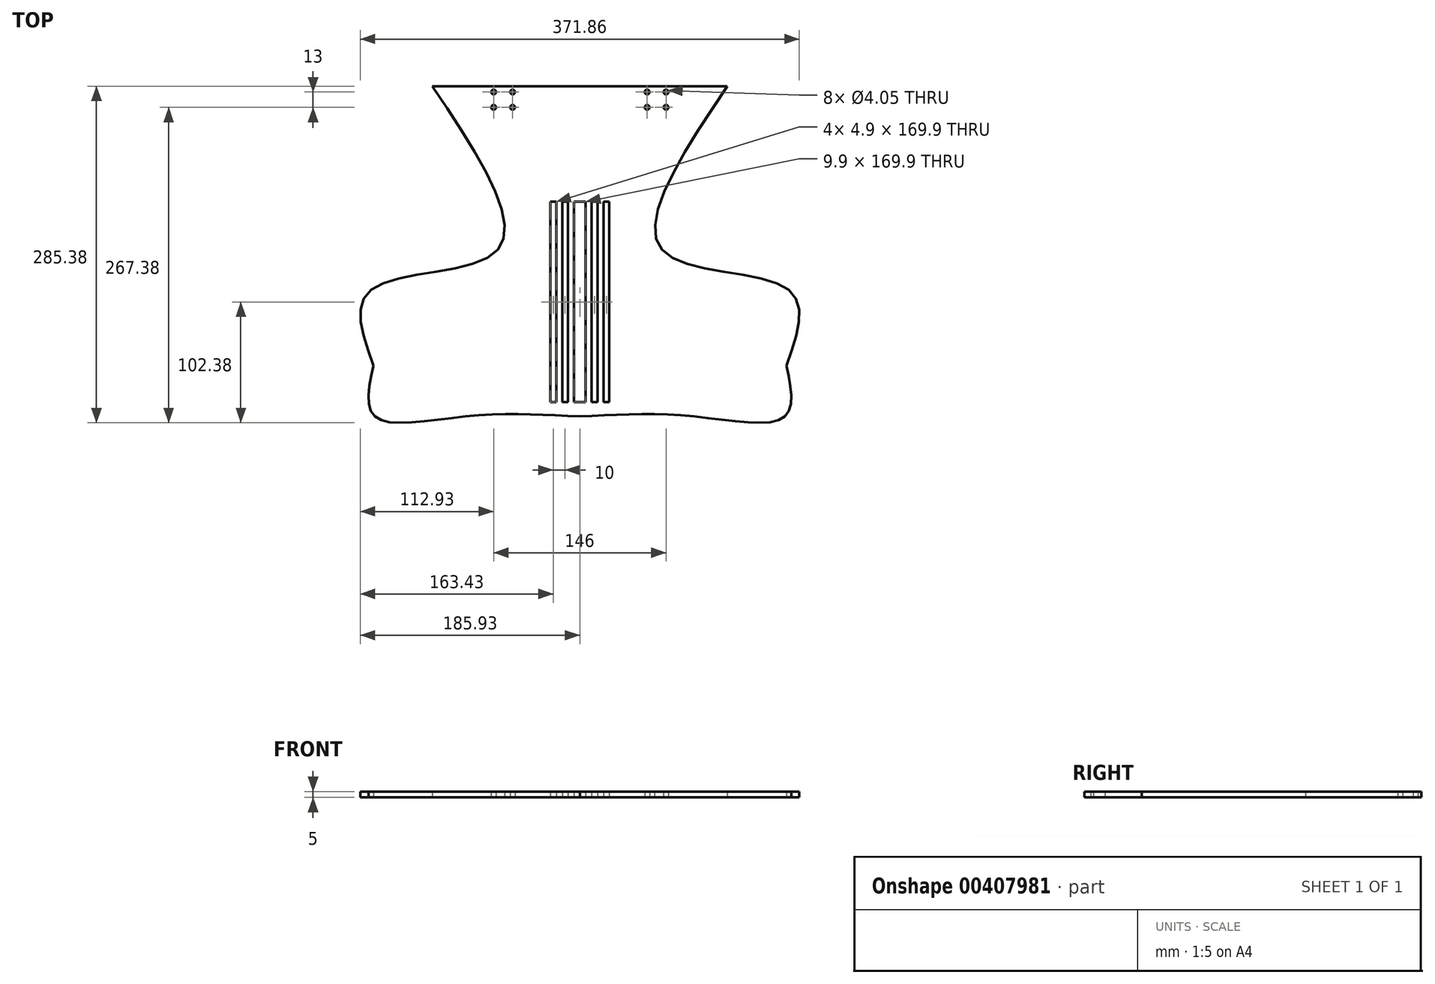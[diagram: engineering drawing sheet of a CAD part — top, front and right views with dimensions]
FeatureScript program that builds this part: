
annotation { "Feature Type Name" : "Feature", "Feature Type Description" : "" }
export const myFeature = defineFeature(function(context is Context, id is Id, definition is map)
    precondition{}
    {
        {
            var Q0;
            Q0=qCreatedBy(makeId("Top.planeOp"),FACE);
            var sketch = newSketch(context, id + "F0", { "sketchPlane" : qUnion([Q0])});
            skLineSegment(sketch, "E0.bottom", {"start": v(-125, 0) * mm, "end": v(125, 0) * mm, "construction": true});
            skLineSegment(sketch, "E0.top", {"start": v(-125, -280) * mm, "end": v(125, -280) * mm, "construction": true});
            skLineSegment(sketch, "E0.left", {"start": v(-125, 0) * mm, "end": v(-125, -280) * mm, "construction": true});
            skLineSegment(sketch, "E0.right", {"start": v(125, 0) * mm, "end": v(125, -280) * mm, "construction": true});
            skFitSpline(sketch, "E1", {"points": [v(-125, 0) * mm, v(-175, -236.88) * mm], "startDerivative": vector(163.58, -419.06) * mm, "endDerivative": vector(5.98, -192.46) * mm});
            skPoint(sketch, "E2", {"position": v(0, -280) * mm});
            skFitSpline(sketch, "E3", {"points": [v(-175, -236.88) * mm, v(0, -280) * mm], "startDerivative": vector(4.02, -129.37) * mm, "endDerivative": vector(290.73, 0) * mm});
            skFitSpline(sketch, "E4.MirrorCS", {"points": [v(125, 0) * mm, v(175, -236.88) * mm], "startDerivative": vector(-163.58, -419.06) * mm, "endDerivative": vector(-5.98, -192.46) * mm});
            skFitSpline(sketch, "E5.MirrorCS", {"points": [v(175, -236.88) * mm, v(0, -280) * mm], "startDerivative": vector(-4.02, -129.37) * mm, "endDerivative": vector(-290.73, 0) * mm});
            skFitSpline(sketch, "E6", {"points": [v(-125, 0) * mm, v(0, 25) * mm], "startDerivative": vector(-31, 79.42) * mm, "endDerivative": vector(148.36, 0.98) * mm});
            skFitSpline(sketch, "E7.MirrorCS", {"points": [v(125, 0) * mm, v(0, 25) * mm], "startDerivative": vector(31, 79.42) * mm, "endDerivative": vector(-148.36, 0.98) * mm});
            skLineSegment(sketch, "E8.bottom", {"start": v(-10, -88) * mm, "end": v(-5, -88) * mm, "construction": true});
            skLineSegment(sketch, "E8.top", {"start": v(-10, -278) * mm, "end": v(-5, -278) * mm, "construction": true});
            skLineSegment(sketch, "E8.left", {"start": v(-10, -88) * mm, "end": v(-10, -278) * mm, "construction": true});
            skLineSegment(sketch, "E8.right", {"start": v(-5, -88) * mm, "end": v(-5, -278) * mm, "construction": true});
            skLineSegment(sketch, "E9.1.0.0", {"start": v(-20, -88) * mm, "end": v(-20, -278) * mm, "construction": true});
            skLineSegment(sketch, "E9.1.0.1", {"start": v(-15, -88) * mm, "end": v(-15, -278) * mm, "construction": true});
            skLineSegment(sketch, "E9.1.0.2", {"start": v(-20, -88) * mm, "end": v(-15, -88) * mm, "construction": true});
            skLineSegment(sketch, "E9.1.0.3", {"start": v(-20, -278) * mm, "end": v(-15, -278) * mm, "construction": true});
            skLineSegment(sketch, "E9.2.0.0", {"start": v(-30, -88) * mm, "end": v(-30, -278) * mm, "construction": true});
            skLineSegment(sketch, "E9.2.0.1", {"start": v(-25, -88) * mm, "end": v(-25, -278) * mm, "construction": true});
            skLineSegment(sketch, "E9.2.0.2", {"start": v(-30, -88) * mm, "end": v(-25, -88) * mm, "construction": true});
            skLineSegment(sketch, "E9.2.0.3", {"start": v(-30, -278) * mm, "end": v(-25, -278) * mm, "construction": true});
            skLineSegment(sketch, "E9.direction1", {"start": v(-10, -278) * mm, "end": v(-20, -278) * mm, "construction": true});
            skLineSegment(sketch, "E10.MirrorCS", {"start": v(10, -278) * mm, "end": v(20, -278) * mm, "construction": true});
            skLineSegment(sketch, "E11.MirrorCS", {"start": v(20, -278) * mm, "end": v(15, -278) * mm, "construction": true});
            skLineSegment(sketch, "E12.MirrorCS", {"start": v(10, -278) * mm, "end": v(5, -278) * mm, "construction": true});
            skLineSegment(sketch, "E13.MirrorCS", {"start": v(20, -88) * mm, "end": v(15, -88) * mm, "construction": true});
            skLineSegment(sketch, "E14.MirrorCS", {"start": v(30, -278) * mm, "end": v(25, -278) * mm, "construction": true});
            skLineSegment(sketch, "E15.MirrorCS", {"start": v(10, -88) * mm, "end": v(5, -88) * mm, "construction": true});
            skLineSegment(sketch, "E16.MirrorCS", {"start": v(30, -88) * mm, "end": v(25, -88) * mm, "construction": true});
            skLineSegment(sketch, "E17.MirrorCS", {"start": v(30, -88) * mm, "end": v(30, -278) * mm, "construction": true});
            skLineSegment(sketch, "E18.MirrorCS", {"start": v(10, -88) * mm, "end": v(10, -278) * mm, "construction": true});
            skLineSegment(sketch, "E19.MirrorCS", {"start": v(15, -88) * mm, "end": v(15, -278) * mm, "construction": true});
            skLineSegment(sketch, "E20.MirrorCS", {"start": v(5, -88) * mm, "end": v(5, -278) * mm, "construction": true});
            skLineSegment(sketch, "E21.MirrorCS", {"start": v(20, -88) * mm, "end": v(20, -278) * mm, "construction": true});
            skLineSegment(sketch, "E22.MirrorCS", {"start": v(25, -88) * mm, "end": v(25, -278) * mm, "construction": true});
            skLineSegment(sketch, "E23.bottom", {"start": v(-73, -5) * mm, "end": v(-57, -5) * mm, "construction": true});
            skLineSegment(sketch, "E23.top", {"start": v(-73, -18) * mm, "end": v(-57, -18) * mm, "construction": true});
            skLineSegment(sketch, "E23.left", {"start": v(-73, -5) * mm, "end": v(-73, -18) * mm, "construction": true});
            skLineSegment(sketch, "E23.right", {"start": v(-57, -5) * mm, "end": v(-57, -18) * mm, "construction": true});
            skCircle(sketch, "E24", {"center": v(-73, -5) * mm, "radius": 2.02 * mm, "construction": true});
            skCircle(sketch, "E25", {"center": v(-57, -5) * mm, "radius": 2.02 * mm, "construction": true});
            skCircle(sketch, "E26", {"center": v(-57, -18) * mm, "radius": 2.02 * mm, "construction": true});
            skCircle(sketch, "E27", {"center": v(-73, -18) * mm, "radius": 2.02 * mm, "construction": true});
            skPoint(sketch, "E28", {"position": v(-65, -5) * mm});
            skLineSegment(sketch, "E29.MirrorCS", {"start": v(73, -18) * mm, "end": v(57, -18) * mm, "construction": true});
            skCircle(sketch, "E30.MirrorC", {"center": v(57, -5) * mm, "radius": 2.02 * mm, "construction": true});
            skCircle(sketch, "E31.MirrorC", {"center": v(57, -18) * mm, "radius": 2.02 * mm, "construction": true});
            skPoint(sketch, "E32.MirrorP", {"position": v(65, -5) * mm});
            skCircle(sketch, "E33.MirrorC", {"center": v(73, -5) * mm, "radius": 2.02 * mm, "construction": true});
            skLineSegment(sketch, "E34.MirrorCS", {"start": v(73, -5) * mm, "end": v(57, -5) * mm, "construction": true});
            skLineSegment(sketch, "E35.MirrorCS", {"start": v(57, -5) * mm, "end": v(57, -18) * mm, "construction": true});
            skCircle(sketch, "E36.MirrorC", {"center": v(73, -18) * mm, "radius": 2.02 * mm, "construction": true});
            skLineSegment(sketch, "E37.MirrorCS", {"start": v(73, -5) * mm, "end": v(73, -18) * mm, "construction": true});
            skSolve(sketch);
        }
        {
            var Q0;
            Q0=qCreatedBy(makeId("Top.planeOp"),FACE);
            var sketch = newSketch(context, id + "F1", { "sketchPlane" : qUnion([Q0])});
            skFitSpline(sketch, "E38.0", {"points": [v(-125, 0) * mm, v(-70.47, -139.69) * mm, v(-177, -172.72) * mm, v(-175, -236.88) * mm]});
            skFitSpline(sketch, "E38.1", {"points": [v(-175, -236.88) * mm, v(-173.66, -280) * mm, v(-96.91, -280) * mm, v(0, -280) * mm]});
            skFitSpline(sketch, "E38.2", {"points": [v(175, -236.88) * mm, v(173.66, -280) * mm, v(96.91, -280) * mm, v(0, -280) * mm]});
            skFitSpline(sketch, "E38.3", {"points": [v(125, 0) * mm, v(70.47, -139.69) * mm, v(177, -172.72) * mm, v(175, -236.88) * mm]});
            skLineSegment(sketch, "E38.4", {"start": v(-125, 0) * mm, "end": v(125, 0) * mm});
            skCircle(sketch, "E39.0", {"center": v(57, -18) * mm, "radius": 2.02 * mm});
            skCircle(sketch, "E39.1", {"center": v(73, -18) * mm, "radius": 2.02 * mm});
            skCircle(sketch, "E39.2", {"center": v(73, -5) * mm, "radius": 2.02 * mm});
            skCircle(sketch, "E39.3", {"center": v(57, -5) * mm, "radius": 2.02 * mm});
            skCircle(sketch, "E39.4", {"center": v(-73, -18) * mm, "radius": 2.02 * mm});
            skCircle(sketch, "E39.5", {"center": v(-57, -18) * mm, "radius": 2.02 * mm});
            skCircle(sketch, "E39.6", {"center": v(-57, -5) * mm, "radius": 2.02 * mm});
            skCircle(sketch, "E39.7", {"center": v(-73, -5) * mm, "radius": 2.02 * mm});
            skLineSegment(sketch, "E40.bottom", {"start": v(-25, -98) * mm, "end": v(-20, -98) * mm, "construction": true});
            skLineSegment(sketch, "E40.top", {"start": v(-25, -268) * mm, "end": v(-20, -268) * mm, "construction": true});
            skLineSegment(sketch, "E40.left", {"start": v(-25, -98) * mm, "end": v(-25, -268) * mm, "construction": true});
            skLineSegment(sketch, "E40.right", {"start": v(-20, -98) * mm, "end": v(-20, -268) * mm, "construction": true});
            skLineSegment(sketch, "E41.bottom", {"start": v(-15, -98) * mm, "end": v(-10, -98) * mm, "construction": true});
            skLineSegment(sketch, "E41.top", {"start": v(-15, -268) * mm, "end": v(-10, -268) * mm, "construction": true});
            skLineSegment(sketch, "E41.left", {"start": v(-15, -98) * mm, "end": v(-15, -268) * mm, "construction": true});
            skLineSegment(sketch, "E41.right", {"start": v(-10, -98) * mm, "end": v(-10, -268) * mm, "construction": true});
            skLineSegment(sketch, "E42.bottom", {"start": v(-5, -98) * mm, "end": v(5, -98) * mm, "construction": true});
            skLineSegment(sketch, "E42.top", {"start": v(-5, -268) * mm, "end": v(5, -268) * mm, "construction": true});
            skLineSegment(sketch, "E42.left", {"start": v(-5, -98) * mm, "end": v(-5, -268) * mm, "construction": true});
            skLineSegment(sketch, "E42.right", {"start": v(5, -98) * mm, "end": v(5, -268) * mm, "construction": true});
            skLineSegment(sketch, "E43.bottom", {"start": v(10, -98) * mm, "end": v(15, -98) * mm, "construction": true});
            skLineSegment(sketch, "E43.top", {"start": v(10, -268) * mm, "end": v(15, -268) * mm, "construction": true});
            skLineSegment(sketch, "E43.left", {"start": v(10, -98) * mm, "end": v(10, -268) * mm, "construction": true});
            skLineSegment(sketch, "E43.right", {"start": v(15, -98) * mm, "end": v(15, -268) * mm, "construction": true});
            skLineSegment(sketch, "E44.bottom", {"start": v(20, -98) * mm, "end": v(25, -98) * mm, "construction": true});
            skLineSegment(sketch, "E44.top", {"start": v(20, -268) * mm, "end": v(25, -268) * mm, "construction": true});
            skLineSegment(sketch, "E44.left", {"start": v(20, -98) * mm, "end": v(20, -268) * mm, "construction": true});
            skLineSegment(sketch, "E44.right", {"start": v(25, -98) * mm, "end": v(25, -268) * mm, "construction": true});
            skLineSegment(sketch, "E45.0", {"start": v(-24.95, -98.05) * mm, "end": v(-20.05, -98.05) * mm});
            skLineSegment(sketch, "E45.1", {"start": v(-24.95, -98.05) * mm, "end": v(-24.95, -267.95) * mm});
            skLineSegment(sketch, "E45.2", {"start": v(-24.95, -267.95) * mm, "end": v(-20.05, -267.95) * mm});
            skLineSegment(sketch, "E45.3", {"start": v(-20.05, -98.05) * mm, "end": v(-20.05, -267.95) * mm});
            skPoint(sketch, "E46", {"position": v(-25, -183) * mm});
            skLineSegment(sketch, "E47.0", {"start": v(-30, -88) * mm, "end": v(-30, -278) * mm, "construction": true});
            skLineSegment(sketch, "E47.1", {"start": v(-25, -88) * mm, "end": v(-25, -278) * mm, "construction": true});
            skLineSegment(sketch, "E47.2", {"start": v(-30, -88) * mm, "end": v(-25, -88) * mm, "construction": true});
            skLineSegment(sketch, "E47.3", {"start": v(-20, -88) * mm, "end": v(-20, -278) * mm, "construction": true});
            skLineSegment(sketch, "E47.4", {"start": v(-20, -88) * mm, "end": v(-15, -88) * mm, "construction": true});
            skLineSegment(sketch, "E47.5", {"start": v(-15, -88) * mm, "end": v(-15, -278) * mm, "construction": true});
            skLineSegment(sketch, "E47.6", {"start": v(-10, -88) * mm, "end": v(-10, -278) * mm, "construction": true});
            skLineSegment(sketch, "E47.7", {"start": v(-10, -88) * mm, "end": v(-5, -88) * mm, "construction": true});
            skLineSegment(sketch, "E47.8", {"start": v(-5, -88) * mm, "end": v(-5, -278) * mm, "construction": true});
            skLineSegment(sketch, "E47.9", {"start": v(5, -88) * mm, "end": v(5, -278) * mm, "construction": true});
            skLineSegment(sketch, "E47.10", {"start": v(10, -88) * mm, "end": v(5, -88) * mm, "construction": true});
            skLineSegment(sketch, "E47.11", {"start": v(10, -88) * mm, "end": v(10, -278) * mm, "construction": true});
            skLineSegment(sketch, "E47.12", {"start": v(15, -88) * mm, "end": v(15, -278) * mm, "construction": true});
            skLineSegment(sketch, "E47.13", {"start": v(20, -88) * mm, "end": v(15, -88) * mm, "construction": true});
            skLineSegment(sketch, "E47.14", {"start": v(20, -88) * mm, "end": v(20, -278) * mm, "construction": true});
            skLineSegment(sketch, "E47.15", {"start": v(25, -88) * mm, "end": v(25, -278) * mm, "construction": true});
            skLineSegment(sketch, "E47.16", {"start": v(30, -88) * mm, "end": v(25, -88) * mm, "construction": true});
            skLineSegment(sketch, "E47.17", {"start": v(30, -88) * mm, "end": v(30, -278) * mm, "construction": true});
            skLineSegment(sketch, "E47.18", {"start": v(-10, -278) * mm, "end": v(-5, -278) * mm, "construction": true});
            skLineSegment(sketch, "E47.19", {"start": v(-10, -278) * mm, "end": v(-20, -278) * mm, "construction": true});
            skLineSegment(sketch, "E47.20", {"start": v(-30, -278) * mm, "end": v(-25, -278) * mm, "construction": true});
            skLineSegment(sketch, "E47.21", {"start": v(10, -278) * mm, "end": v(5, -278) * mm, "construction": true});
            skLineSegment(sketch, "E47.22", {"start": v(10, -278) * mm, "end": v(20, -278) * mm, "construction": true});
            skLineSegment(sketch, "E47.23", {"start": v(30, -278) * mm, "end": v(25, -278) * mm, "construction": true});
            skPoint(sketch, "E48", {"position": v(-20, -183) * mm});
            skPoint(sketch, "E49", {"position": v(-15, -183) * mm});
            skPoint(sketch, "E50", {"position": v(-10, -183) * mm});
            skPoint(sketch, "E51", {"position": v(-5, -183) * mm});
            skPoint(sketch, "E52", {"position": v(5, -183) * mm});
            skPoint(sketch, "E53.positionSnap0", {"position": v(10, -183) * mm});
            skPoint(sketch, "E54", {"position": v(15, -183) * mm});
            skPoint(sketch, "E55", {"position": v(20, -183) * mm});
            skPoint(sketch, "E56", {"position": v(25, -183) * mm});
            skLineSegment(sketch, "E57.0", {"start": v(-14.95, -267.95) * mm, "end": v(-10.05, -267.95) * mm});
            skLineSegment(sketch, "E57.1", {"start": v(-14.95, -98.05) * mm, "end": v(-14.95, -267.95) * mm});
            skLineSegment(sketch, "E57.2", {"start": v(-14.95, -98.05) * mm, "end": v(-10.05, -98.05) * mm});
            skLineSegment(sketch, "E57.3", {"start": v(-10.05, -98.05) * mm, "end": v(-10.05, -267.95) * mm});
            skLineSegment(sketch, "E58.0", {"start": v(-4.95, -267.95) * mm, "end": v(4.95, -267.95) * mm});
            skLineSegment(sketch, "E58.1", {"start": v(-4.95, -98.05) * mm, "end": v(-4.95, -267.95) * mm});
            skLineSegment(sketch, "E58.2", {"start": v(-4.95, -98.05) * mm, "end": v(4.95, -98.05) * mm});
            skLineSegment(sketch, "E58.3", {"start": v(4.95, -98.05) * mm, "end": v(4.95, -267.95) * mm});
            skLineSegment(sketch, "E59.0", {"start": v(10.05, -267.95) * mm, "end": v(14.95, -267.95) * mm});
            skLineSegment(sketch, "E59.1", {"start": v(10.05, -98.05) * mm, "end": v(10.05, -267.95) * mm});
            skLineSegment(sketch, "E59.2", {"start": v(10.05, -98.05) * mm, "end": v(14.95, -98.05) * mm});
            skLineSegment(sketch, "E59.3", {"start": v(14.95, -98.05) * mm, "end": v(14.95, -267.95) * mm});
            skLineSegment(sketch, "E60.0", {"start": v(20.05, -267.95) * mm, "end": v(24.95, -267.95) * mm});
            skLineSegment(sketch, "E60.1", {"start": v(20.05, -98.05) * mm, "end": v(20.05, -267.95) * mm});
            skLineSegment(sketch, "E60.2", {"start": v(20.05, -98.05) * mm, "end": v(24.95, -98.05) * mm});
            skLineSegment(sketch, "E60.3", {"start": v(24.95, -98.05) * mm, "end": v(24.95, -267.95) * mm});
            skSolve(sketch);
        }
        {
            var Q0;
            Q0 = qSketchRegion(id + "F1", true);
            extrude(context, id + "F2", {"entities" : qUnion([Q0]), "depth" : 5 * mm});
        }
    });
